# Revit family: QF_BOURGEAT_Satellite4GT_chaud_1-1_entree325_vitree_ouverture_gauche
name_source: partatom
category: Equipement spécialisé
revit_build: Autodesk Revit 2015 (Build: 20140606_1530(x64)
units: mm (PartAtom-declared; Revit-internal decimal feet)

## types (2) — shared parameters
Certification = NF hygiene alimentaire
Charge max = 170.00 kg
Consommation énergétique = 0.77 Kwh/h NFD40-016
Diametre_roue = 160 mm  [stored 0.524934 ft]
Fabricant = BOURGEAT
Fréquence = 50 Hz
Hauteur hors tout = 1575 mm  [stored 5.16732 ft]
Hauteur_poignee_porte_sol = 548 mm  [stored 1.7979 ft]
Hauteur_poignees_laterales = 930 mm  [stored 3.05118 ft]
Hauteur_porte = 1328 mm  [stored 4.35696 ft]
Hauteur_roue = 200 mm  [stored 0.656168 ft]
Indice de protection = IP25
Intensité nominale = 8 A
Largeur_porte = 500 mm  [stored 1.64042 ft]
Longueur hors tout = 585 mm  [stored 1.91929 ft]
Longueur_poignees_laterales = 688 mm  [stored 2.25722 ft]
Materiau_Poignee_porte = B_Elastomère_TPE_S
Materiau_bac = B_Elastomère_TPE_S
Materiau_bandage = B_Elastomère_TPE_S
Materiau_porte = Acier inoxydable, brossé
Materiau_vitre = Verre, vitrage transparent, trempé
Materiaux_reserve_eau = Acrylique, transparent
Nature isolant = Mousse sans PU
Phase = 2
Poids net à vide = 90.00 kg
Poignee_gauche = Oui
Pos_IHM_bord_gauche_porte_gauche = 150 mm
Pos_V_IHM = 98 mm  [stored 0.321522 ft]
Pos_vitre_bord_gauche_porte_gauche = 300 mm
Profondeur hors tout = 844 mm  [stored 2.76903 ft]
Puissance électrique  = 1750 W
Spécification du Fabricant = Satellite 4GT
Tension = 230 V
URL catalogue = http://www.bourgeat.fr

## per-type parameters (varying)
| type | Humidification | Modèle |
| GN17_humidification_tirant_gauche | Oui | 841717 |
| GN17_sans_humidification_tirant_gauche | Non | 841517 |

note: [stored X ft] marks values corroborated as IEEE doubles in the binary element streams (Revit-internal decimal feet)
